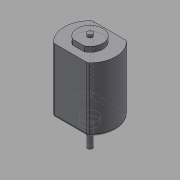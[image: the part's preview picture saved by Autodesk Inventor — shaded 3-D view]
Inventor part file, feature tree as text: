
AUTODESK INVENTOR PART (.ipt)
format: ipt  version: 2015 (Build 190159000, 159)  size: 114,176 bytes
history: native  units: in
note: dims shown in document units (in); Inventor stores cm internally (conversion verified against a paired STEP export)
features: sketch x5, other x3
ambient origin geometry x8: Origin, YZ Plane, XZ Plane, XY Plane, X Axis, Y Axis, Z Axis, Center Point
bodies: Solid1 (feature_tree)
feature tree (8):
  other  "motor.ipt"
  other  "Solid1::motor.ipt"
  other  "TaggingFeature1"
  sketch  "Sketch1"  dims[d0=0.3937in]
  sketch  "Sketch2"
  sketch  "Sketch3"
  sketch  "Sketch4"
  sketch  "Sketch5"
